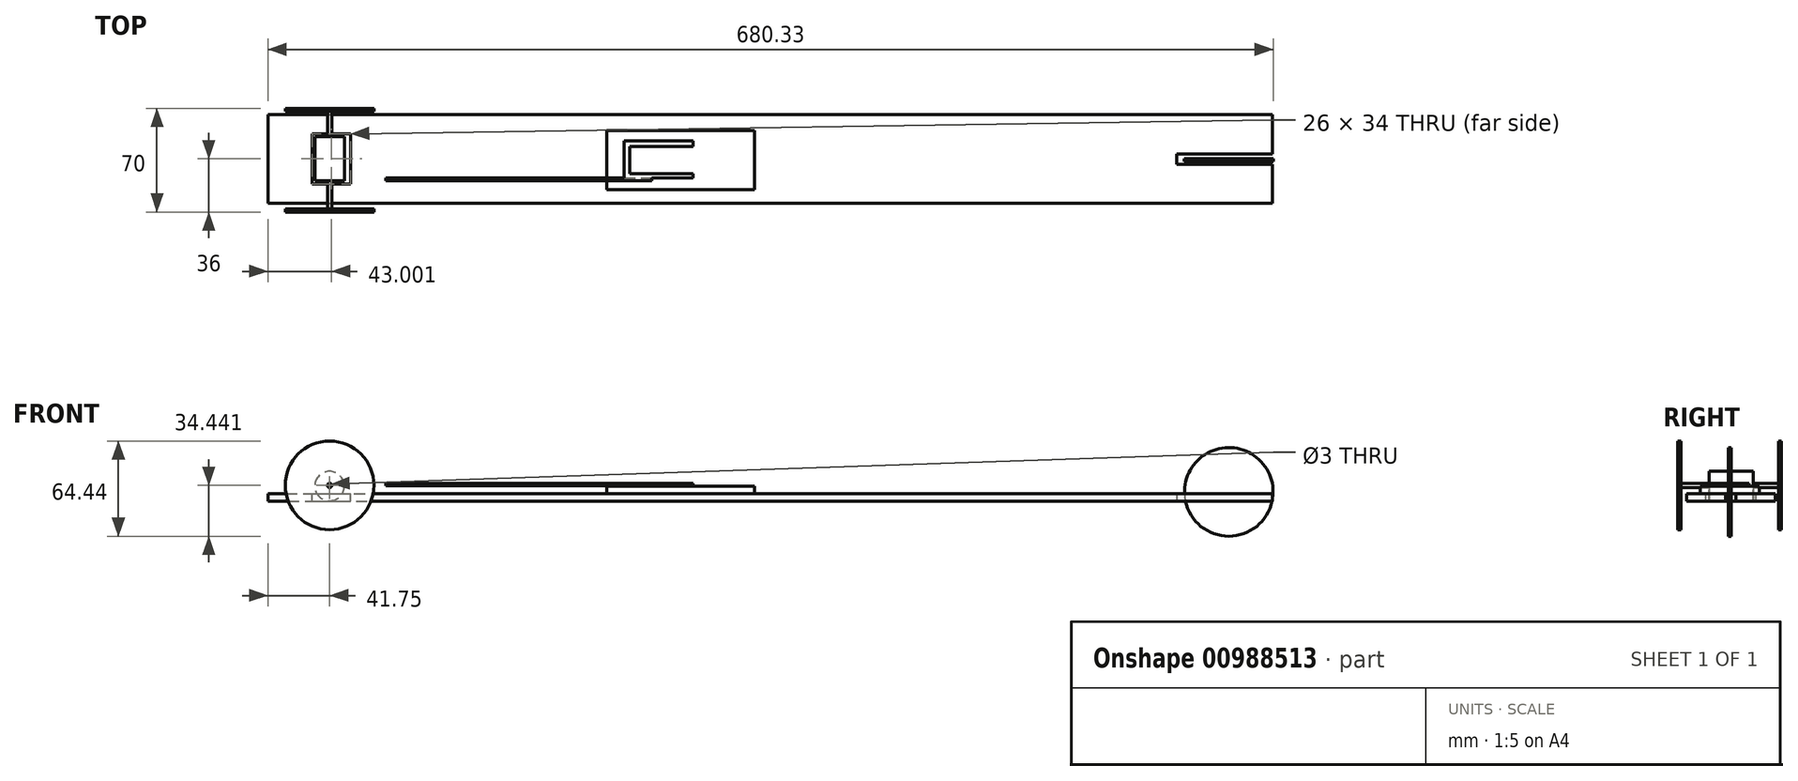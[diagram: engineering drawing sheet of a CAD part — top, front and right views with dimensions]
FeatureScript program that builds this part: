
annotation { "Feature Type Name" : "Feature", "Feature Type Description" : "" }
export const myFeature = defineFeature(function(context is Context, id is Id, definition is map)
    precondition{}
    {
        {
            var Q0;
            Q0=qCreatedBy(makeId("Front.planeOp"),FACE);
            var sketch = newSketch(context, id + "F0", { "sketchPlane" : qUnion([Q0])});
            skLineSegment(sketch, "E0.bottom", {"start": v(-186.6, 6.56) * mm, "end": v(493.4, 6.56) * mm});
            skLineSegment(sketch, "E0.top", {"start": v(-186.6, 1.56) * mm, "end": v(493.4, 1.56) * mm});
            skLineSegment(sketch, "E0.left", {"start": v(-186.6, 6.56) * mm, "end": v(-186.6, 1.56) * mm});
            skLineSegment(sketch, "E0.right", {"start": v(493.4, 6.56) * mm, "end": v(493.4, 1.56) * mm});
            skSolve(sketch);
        }
        {
            var Q0;
            Q0=makeQuery(id+"F0.imprint","IMPRINT",FACE,{"disambiguationData":[TD([[makeQuery(id+"F0.imprint","IMPRINT",EDGE,{"derivedFrom":sQuery(id+"F0.wireOp",EDGE,"E0.bottom")}),-1.0]])]});
            extrude(context, id + "F1", {"entities" : qUnion([Q0]), "depth" : 60 * mm, "offsetDistance" : 25 * mm, "symmetric" : true});
        }
        {
            var Q0;
            Q0=makeQuery(id+"F1.opExtrude","SWEPT_FACE",FACE,{"disambiguationData":[OSD([sQuery(id+"F0.wireOp",EDGE,"E0.right")])]});
            var sketch = newSketch(context, id + "F2", { "sketchPlane" : qUnion([Q0])});
            skLineSegment(sketch, "E1.bottom", {"start": v(-3.73, 6.56) * mm, "end": v(3.27, 6.56) * mm});
            skLineSegment(sketch, "E1.top", {"start": v(-3.73, 1.56) * mm, "end": v(3.27, 1.56) * mm});
            skLineSegment(sketch, "E1.left", {"start": v(-3.73, 6.56) * mm, "end": v(-3.73, 1.56) * mm});
            skLineSegment(sketch, "E1.right", {"start": v(3.27, 6.56) * mm, "end": v(3.27, 1.56) * mm});
            skSolve(sketch);
        }
        {
            var Q0;
            Q0=makeQuery(id+"F2.imprint","IMPRINT",FACE,{"disambiguationData":[TD([[makeQuery(id+"F2.imprint","IMPRINT",EDGE,{"derivedFrom":sQuery(id+"F2.wireOp",EDGE,"E1.bottom")}),-1.0]])]});
            extrude(context, id + "F3", {"entities" : qUnion([Q0]), "operationType" : NewBodyOperationType.REMOVE, "oppositeDirection" : true, "depth" : 65 * mm, "offsetDistance" : 25 * mm});
        }
        {
            var Q0;
            Q0=makeQuery(id+"F1.opExtrude","SWEPT_FACE",FACE,{"disambiguationData":[OSD([sQuery(id+"F0.wireOp",EDGE,"E0.bottom")])]});
            var sketch = newSketch(context, id + "F4", { "sketchPlane" : qUnion([Q0])});
            skLineSegment(sketch, "E2.bottom", {"start": v(-156.6, 17) * mm, "end": v(-130.6, 17) * mm});
            skLineSegment(sketch, "E2.top", {"start": v(-156.6, -17) * mm, "end": v(-130.6, -17) * mm});
            skLineSegment(sketch, "E2.left", {"start": v(-156.6, 17) * mm, "end": v(-156.6, -17) * mm});
            skLineSegment(sketch, "E2.right", {"start": v(-130.6, 17) * mm, "end": v(-130.6, -17) * mm});
            skSolve(sketch);
        }
        {
            var Q0;
            Q0=makeQuery(id+"F4.imprint","IMPRINT",FACE,{"disambiguationData":[TD([[makeQuery(id+"F4.imprint","IMPRINT",EDGE,{"derivedFrom":sQuery(id+"F4.wireOp",EDGE,"E2.bottom")}),-1.0]])]});
            extrude(context, id + "F5", {"entities" : qUnion([Q0]), "operationType" : NewBodyOperationType.REMOVE, "oppositeDirection" : true, "depth" : 25 * mm, "offsetDistance" : 25 * mm});
        }
        {
            var Q0;
            Q0=qCreatedBy(makeId("Front.planeOp"),FACE);
            var sketch = newSketch(context, id + "F6", { "sketchPlane" : qUnion([Q0])});
            skCircle(sketch, "E3", {"center": v(-144.9, 11.72) * mm, "radius": 10 * mm});
            skSolve(sketch);
        }
        {
            var Q0;
            Q0=makeQuery(id+"F6.imprint","IMPRINT",FACE,{"disambiguationData":[TD([[makeQuery(id+"F6.imprint","IMPRINT",EDGE,{"derivedFrom":sQuery(id+"F6.wireOp",EDGE,"E3")}),1.0]])]});
            extrude(context, id + "F7", {"entities" : qUnion([Q0]), "depth" : 30 * mm, "offsetDistance" : 25 * mm, "symmetric" : true});
        }
        {
            var Q0;
            Q0=qCreatedBy(makeId("Front.planeOp"),FACE);
            var sketch = newSketch(context, id + "F8", { "sketchPlane" : qUnion([Q0])});
            skCircle(sketch, "E4", {"center": v(-144.85, 12.15) * mm, "radius": 1.5 * mm});
            skSolve(sketch);
        }
        {
            var Q0;
            Q0 = qSketchRegion(id + "F8", true);
            extrude(context, id + "F9", {"entities" : qUnion([Q0]), "operationType" : NewBodyOperationType.ADD, "depth" : 68 * mm, "offsetDistance" : 25 * mm, "symmetric" : true});
        }
        {
            var Q0;
            Q0=makeQuery(id+"F9.opExtrude","CAP_FACE",FACE,{"disambiguationData":[OSD([sQuery(id+"F8.wireOp",EDGE,"E4")])],"isStart":false});
            var sketch = newSketch(context, id + "F10", { "sketchPlane" : qUnion([Q0])});
            skCircle(sketch, "E5", {"center": v(-144.85, 12.15) * mm, "radius": 30 * mm});
            skSolve(sketch);
        }
        {
            var Q0;
            Q0=makeQuery(id+"F9.opExtrude","CAP_FACE",FACE,{"disambiguationData":[OSD([sQuery(id+"F8.wireOp",EDGE,"E4")])],"isStart":true});
            var sketch = newSketch(context, id + "F11", { "sketchPlane" : qUnion([Q0])});
            skCircle(sketch, "E6", {"center": v(144.85, 12.15) * mm, "radius": 30 * mm});
            skSolve(sketch);
        }
        {
            var Q0;
            Q0=makeQuery(id+"F11.imprint","IMPRINT",FACE,{"disambiguationData":[TD([[makeQuery(id+"F11.imprint","IMPRINT",EDGE,{"derivedFrom":sQuery(id+"F11.wireOp",EDGE,"E6")}),1.0]])]});
            var Q1;
            Q1=makeQuery(id+"F10.imprint","IMPRINT",FACE,{"disambiguationData":[TD([[makeQuery(id+"F10.imprint","IMPRINT",EDGE,{"derivedFrom":sQuery(id+"F10.wireOp",EDGE,"E5")}),1.0]])]});
            extrude(context, id + "F12", {"entities" : qUnion([Q0, Q1]), "operationType" : NewBodyOperationType.ADD, "oppositeDirection" : true, "depth" : 2 * mm, "offsetDistance" : 25 * mm});
        }
        {
            var Q0;
            Q0=makeQuery(id+"F1.opExtrude","SWEPT_FACE",FACE,{"disambiguationData":[OSD([sQuery(id+"F0.wireOp",EDGE,"E0.bottom")])]});
            var sketch = newSketch(context, id + "F13", { "sketchPlane" : qUnion([Q0])});
            skLineSegment(sketch, "E7.bottom", {"start": v(42.83, 19.09) * mm, "end": v(142.83, 19.09) * mm});
            skLineSegment(sketch, "E7.top", {"start": v(42.83, -20.91) * mm, "end": v(142.83, -20.91) * mm});
            skLineSegment(sketch, "E7.left", {"start": v(42.83, 19.09) * mm, "end": v(42.83, -20.91) * mm});
            skLineSegment(sketch, "E7.right", {"start": v(142.83, 19.09) * mm, "end": v(142.83, -20.91) * mm});
            skSolve(sketch);
        }
        {
            var Q0;
            Q0=makeQuery(id+"F13.imprint","IMPRINT",FACE,{"disambiguationData":[TD([[makeQuery(id+"F13.imprint","IMPRINT",EDGE,{"derivedFrom":sQuery(id+"F13.wireOp",EDGE,"E7.bottom")}),-1.0]])]});
            extrude(context, id + "F14", {"entities" : qUnion([Q0]), "operationType" : NewBodyOperationType.ADD, "depth" : 5 * mm, "offsetDistance" : 25 * mm});
        }
        {
            var Q0;
            Q0=makeQuery(id+"F14.opExtrude","CAP_FACE",FACE,{"disambiguationData":[OSD([sQuery(id+"F13.wireOp",EDGE,"E7.bottom"),sQuery(id+"F13.wireOp",EDGE,"E7.top"),sQuery(id+"F13.wireOp",EDGE,"E7.left"),sQuery(id+"F13.wireOp",EDGE,"E7.right")])],"isStart":false});
            var sketch = newSketch(context, id + "F15", { "sketchPlane" : qUnion([Q0])});
            skLineSegment(sketch, "E8.bottom", {"start": v(54.5, 12.09) * mm, "end": v(101.15, 12.09) * mm});
            skLineSegment(sketch, "E8.top", {"start": v(54.5, -12.91) * mm, "end": v(101.15, -12.91) * mm});
            skLineSegment(sketch, "E8.left", {"start": v(54.5, 12.09) * mm, "end": v(54.5, -12.91) * mm});
            skLineSegment(sketch, "E8.right", {"start": v(101.15, 12.09) * mm, "end": v(101.15, -12.91) * mm});
            skLineSegment(sketch, "E9.bottom", {"start": v(58.38, 8.42) * mm, "end": v(101.15, 8.42) * mm});
            skLineSegment(sketch, "E9.top", {"start": v(58.38, -10.1) * mm, "end": v(101.15, -10.1) * mm});
            skLineSegment(sketch, "E9.left", {"start": v(58.38, 8.42) * mm, "end": v(58.38, -10.1) * mm});
            skLineSegment(sketch, "E9.right", {"start": v(101.15, 8.42) * mm, "end": v(101.15, -10.1) * mm});
            skSolve(sketch);
        }
        {
            var Q0;
            {var subQ1=sQuery(id+"F15.wireOp",EDGE,"E8.bottom");Q0=makeQuery(id+"F15.imprint","IMPRINT",FACE,{"disambiguationData":[TD([[makeQuery(id+"F15.imprint","IMPRINT",EDGE,{"derivedFrom":subQ1}),-1.0]])]});}
            extrude(context, id + "F16", {"entities" : qUnion([Q0]), "operationType" : NewBodyOperationType.ADD, "depth" : 2 * mm, "offsetDistance" : 25 * mm});
        }
        {
            var Q0;
            Q0=makeQuery(id+"F16.opExtrude","SWEPT_FACE",FACE,{"disambiguationData":[OSD([sQuery(id+"F15.wireOp",EDGE,"E8.top")])]});
            var sketch = newSketch(context, id + "F17", { "sketchPlane" : qUnion([Q0])});
            skLineSegment(sketch, "E10.bottom", {"start": v(73.18, 13.56) * mm, "end": v(-106.82, 13.56) * mm});
            skLineSegment(sketch, "E10.top", {"start": v(73.18, 12.06) * mm, "end": v(-106.82, 12.06) * mm});
            skLineSegment(sketch, "E10.left", {"start": v(73.18, 13.56) * mm, "end": v(73.18, 12.06) * mm});
            skLineSegment(sketch, "E10.right", {"start": v(-106.82, 13.56) * mm, "end": v(-106.82, 12.06) * mm});
            skSolve(sketch);
        }
        {
            var Q0;
            {var subQ4=sQuery(id+"F17.wireOp",EDGE,"E10.left");Q0=makeQuery(id+"F17.imprint","IMPRINT",FACE,{"disambiguationData":[TD([[makeQuery(id+"F17.imprint","IMPRINT",EDGE,{"derivedFrom":subQ4}),-1.0]])]});}
            var Q1;
            {var subQ3=sQuery(id+"F17.wireOp",EDGE,"E10.right");Q1=makeQuery(id+"F17.imprint","IMPRINT",FACE,{"disambiguationData":[TD([[makeQuery(id+"F17.imprint","IMPRINT",EDGE,{"derivedFrom":subQ3}),1.0]])]});}
            extrude(context, id + "F18", {"entities" : qUnion([Q0, Q1]), "operationType" : NewBodyOperationType.ADD, "depth" : 2 * mm, "offsetDistance" : 25 * mm});
        }
        {
            var Q0;
            Q0=qCreatedBy(makeId("Front.planeOp"),FACE);
            var sketch = newSketch(context, id + "F19", { "sketchPlane" : qUnion([Q0])});
            skCircle(sketch, "E11", {"center": v(463.73, 7.71) * mm, "radius": 30 * mm});
            skSolve(sketch);
        }
        {
            var Q0;
            Q0=makeQuery(id+"F19.imprint","IMPRINT",FACE,{"disambiguationData":[TD([[makeQuery(id+"F19.imprint","IMPRINT",EDGE,{"derivedFrom":sQuery(id+"F19.wireOp",EDGE,"E11")}),1.0]])]});
            extrude(context, id + "F20", {"entities" : qUnion([Q0]), "depth" : 2 * mm, "offsetDistance" : 25 * mm});
        }
    });
